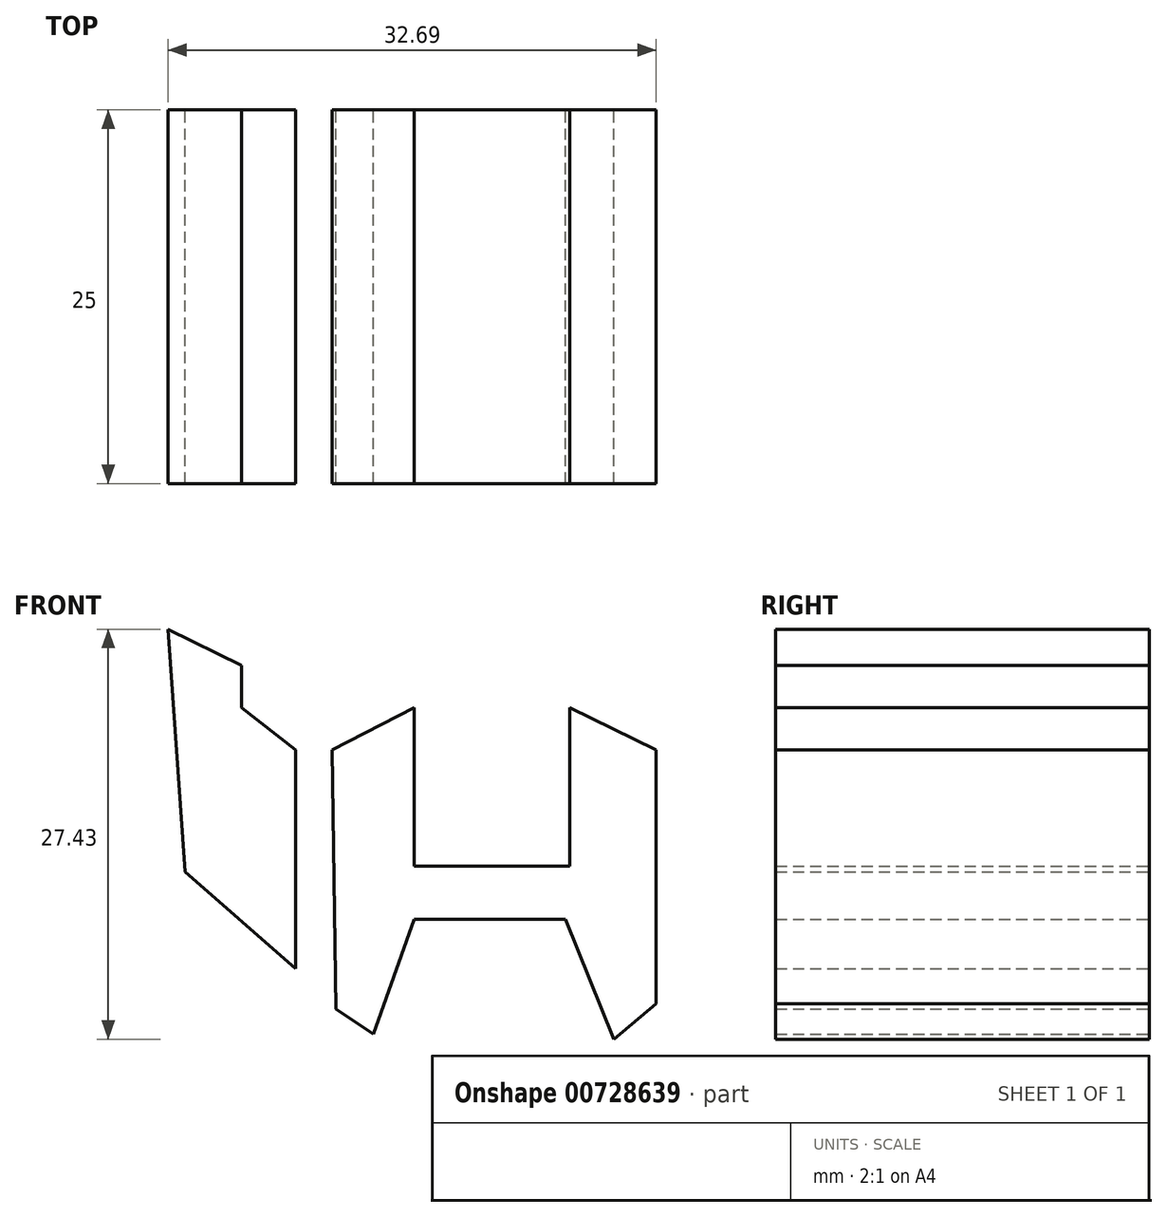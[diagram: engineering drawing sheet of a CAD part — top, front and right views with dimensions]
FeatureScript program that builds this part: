
annotation { "Feature Type Name" : "Feature", "Feature Type Description" : "" }
export const myFeature = defineFeature(function(context is Context, id is Id, definition is map)
    precondition{}
    {
        {
            var Q0;
            Q0=qCreatedBy(makeId("Front.planeOp"),FACE);
            var sketch = newSketch(context, id + "F0", { "sketchPlane" : qUnion([Q0])});
            skLineSegment(sketch, "E0", {"start": v(-16.5, 12.02) * mm, "end": v(-15.36, -4.22) * mm});
            skLineSegment(sketch, "E1", {"start": v(-15.36, -4.22) * mm, "end": v(-7.94, -10.7) * mm});
            skLineSegment(sketch, "E2", {"start": v(-7.94, -10.7) * mm, "end": v(-7.94, 3.93) * mm});
            skLineSegment(sketch, "E3", {"start": v(-7.94, 3.93) * mm, "end": v(-11.58, 6.77) * mm});
            skLineSegment(sketch, "E4", {"start": v(-11.58, 6.77) * mm, "end": v(-11.58, 9.6) * mm});
            skLineSegment(sketch, "E5", {"start": v(-11.58, 9.6) * mm, "end": v(-16.5, 12.02) * mm});
            skLineSegment(sketch, "E6", {"start": v(-5.51, 3.93) * mm, "end": v(0, 6.77) * mm});
            skLineSegment(sketch, "E7", {"start": v(0, 6.77) * mm, "end": v(0, -3.82) * mm});
            skLineSegment(sketch, "E8", {"start": v(0, -3.82) * mm, "end": v(10.4, -3.82) * mm});
            skLineSegment(sketch, "E9", {"start": v(10.4, -3.82) * mm, "end": v(10.4, 6.77) * mm});
            skLineSegment(sketch, "E10", {"start": v(10.4, 6.77) * mm, "end": v(16.2, 3.93) * mm});
            skLineSegment(sketch, "E11", {"start": v(16.2, 3.93) * mm, "end": v(16.2, -13.05) * mm});
            skLineSegment(sketch, "E12", {"start": v(16.2, -13.05) * mm, "end": v(13.36, -15.41) * mm});
            skLineSegment(sketch, "E13", {"start": v(13.36, -15.41) * mm, "end": v(10.13, -7.4) * mm});
            skLineSegment(sketch, "E14", {"start": v(10.13, -7.4) * mm, "end": v(0, -7.4) * mm});
            skLineSegment(sketch, "E15", {"start": v(0, -7.4) * mm, "end": v(-2.75, -15.08) * mm});
            skLineSegment(sketch, "E16", {"start": v(-2.75, -15.08) * mm, "end": v(-5.24, -13.4) * mm});
            skLineSegment(sketch, "E17", {"start": v(-5.24, -13.4) * mm, "end": v(-5.51, 3.93) * mm});
            skSolve(sketch);
        }
        {
            var Q0;
            Q0 = qSketchRegion(id + "F0", true);
            extrude(context, id + "F1", {"entities" : qUnion([Q0]), "depth" : 25 * mm, "offsetDistance" : 25 * mm});
        }
    });
